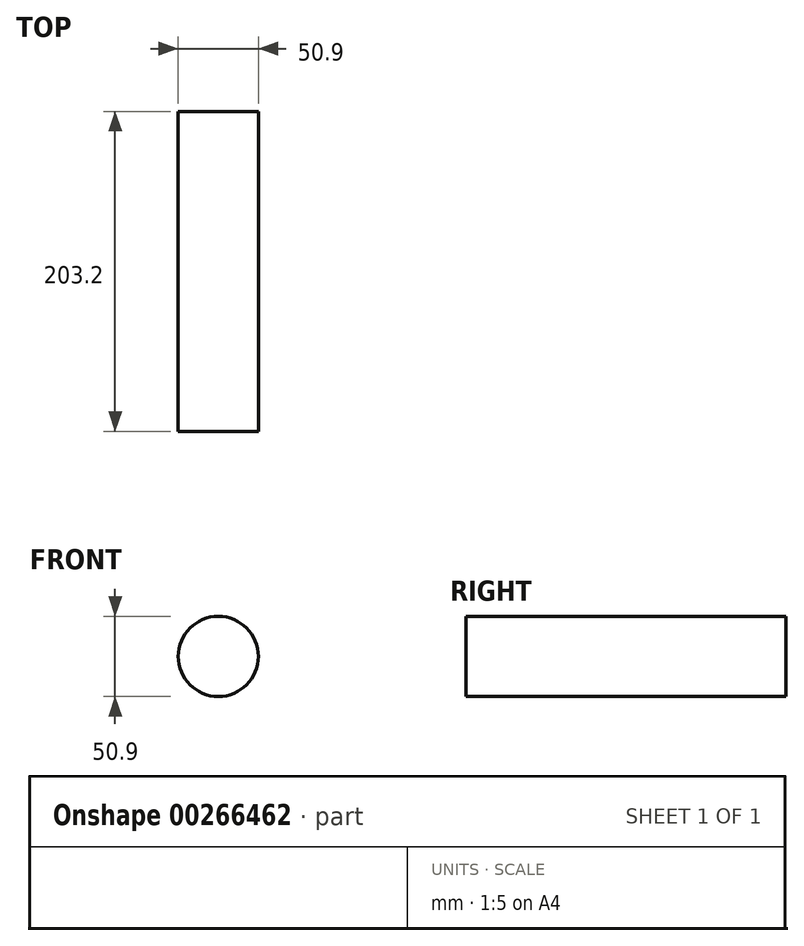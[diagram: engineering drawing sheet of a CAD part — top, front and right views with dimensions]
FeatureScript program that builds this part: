
annotation { "Feature Type Name" : "Feature", "Feature Type Description" : "" }
export const myFeature = defineFeature(function(context is Context, id is Id, definition is map)
    precondition{}
    {
        {
            var Q0;
            Q0=qCreatedBy(makeId("Front.planeOp"),FACE);
            var sketch = newSketch(context, id + "F0", { "sketchPlane" : qUnion([Q0])});
            skCircle(sketch, "E0", {"center": v(0, 0) * mm, "radius": 25.45 * mm});
            skSolve(sketch);
        }
        {
            var Q0;
            Q0=makeQuery(id+"F0.imprint","IMPRINT",FACE,{"disambiguationData":[TD([[makeQuery(id+"F0.imprint","IMPRINT",EDGE,{"derivedFrom":sQuery(id+"F0.wireOp",EDGE,"E0")}),1.0]])]});
            extrude(context, id + "F1", {"entities" : qUnion([Q0]), "depth" : 203.2 * mm});
        }
    });
